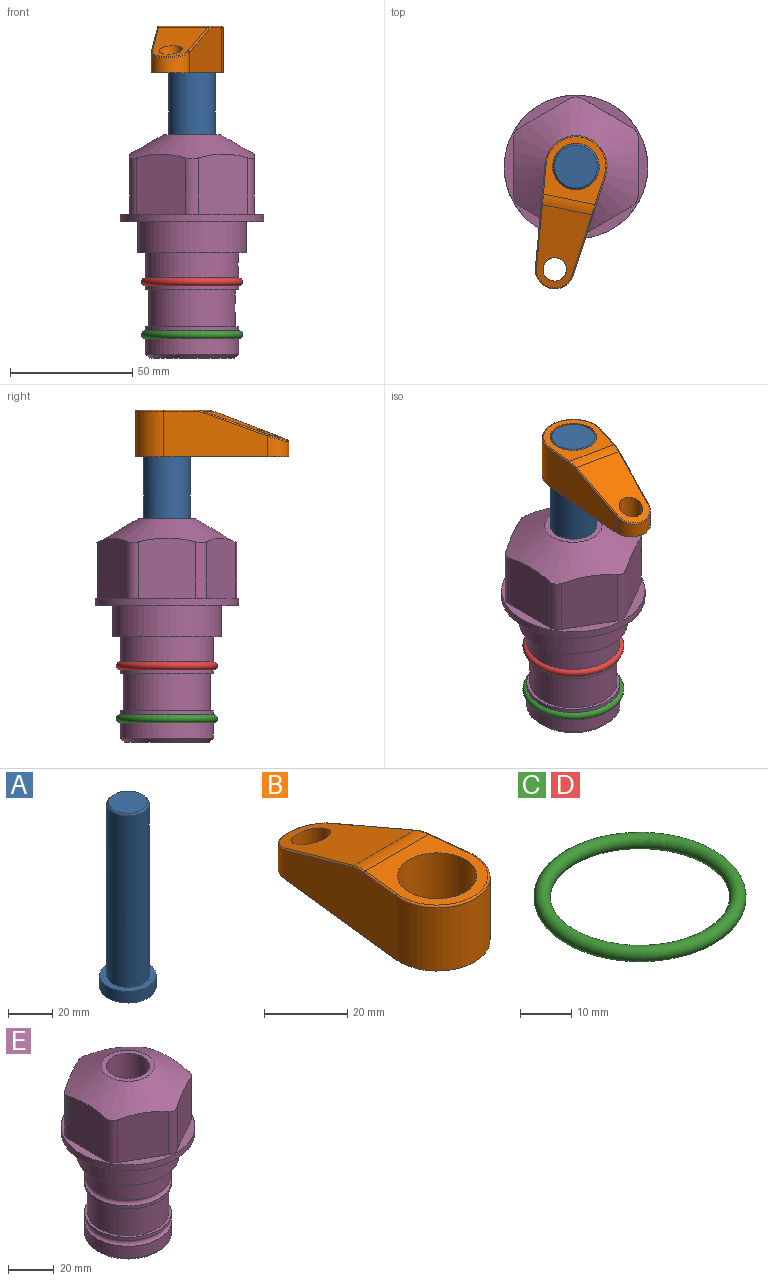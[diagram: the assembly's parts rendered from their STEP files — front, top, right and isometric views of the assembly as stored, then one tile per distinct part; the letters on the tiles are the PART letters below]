
ASSEMBLY  parts=5 mates=3
PART A: 6 faces, bbox 25.4x25.4x101.6 mm
  f0: plane 17.46x17.46mm, normal (0,0,1), area 239.5mm2, adj f5
  f1: plane 25.4x25.4mm, normal (0,0,-1), area 506.7mm2, adj f2
  f2: cylinder r=12.7mm len=25.4mm, axis (0,0,1), area 506.7mm2, adj f1,f3
  f3: plane 25.4x25.4mm, normal (0,0,1), area 221.7mm2, adj f2,f4
  f4: cylinder r=9.53mm len=94.46mm, axis (0,0,1), area 5653mm2, adj f3,f5
  f5: cone r=8.73mm half-angle=45deg, axis (0,0,-1), area 64.4mm2, adj f0,f4
PART B: 44 faces, bbox 27.5x64.5x19.1 mm
  f0: plane 2.3x0.95mm, normal (0,0,-1), area 1mm2, adj f25,f30,f34
  f1: plane 63.5x25.4mm, normal (0,0,-1), area 561.7mm2, adj f2,f3,f4,f5,f6,f7,f19,f20
  f2: cylinder r=12.7mm len=25.4mm, axis (0,0,-1), area 792.2mm2, adj f1,f3,f5,f13
  f3: plane 42.33x18.54mm, normal (0.99,0.11,0), area 647mm2, adj f1,f2,f4,f11,f12,f14
  f4: cylinder r=7.94mm len=15.78mm, axis (0,0,-1), area 158.6mm2, adj f1,f3,f5,f16
  f5: plane 42.33x18.54mm, normal (-0.99,0.11,0), area 647mm2, adj f1,f2,f4,f15,f17,f18
  f6: cylinder r=9.53mm len=19.05mm, axis (0,0,-1), area 1140.1mm2, adj f1,f8
  f7: cylinder r=4.76mm len=10.98mm, axis (0,0,-1), area 276.1mm2, adj f1,f9
  f8: plane 25.83x24.38mm, normal (0,0,1), area 262.2mm2, adj f6,f10,f11,f13,f15
  f9: plane 32.49x20.55mm, normal (0,0.34,0.94), area 489.9mm2, adj f7,f10,f14,f16,f18
  f10: cylinder r=12.7mm len=21.49mm, axis (-1,0,0), area 93.2mm2, adj f8,f9,f12,f17
  f11: cylinder r=0.51mm len=12.34mm, axis (0.11,-0.99,0), area 9.9mm2, adj f3,f8,f12,f13
  f12: bspline ~7.62x1.64mm, area 3.5mm2, adj f3,f10,f11,f14
  f13: torus R=12.19mm, axis (0,0,1), area 33.6mm2, adj f2,f8,f11,f15
  f14: cylinder r=0.51mm len=26.01mm, axis (0.1,-0.93,0.34), area 21.6mm2, adj f3,f9,f12,f16
  f15: cylinder r=0.51mm len=12.34mm, axis (0.11,0.99,0), area 9.9mm2, adj f5,f8,f13,f17
  f16: bspline ~15.78x7.05mm, area 15.7mm2, adj f4,f9,f14,f18
  f17: bspline ~7.62x1.64mm, area 3.5mm2, adj f5,f10,f15,f18
  f18: cylinder r=0.51mm len=26.01mm, axis (0.1,0.93,-0.34), area 21.6mm2, adj f5,f9,f16,f17
  f19: plane 21.6x14.29mm, normal (-0.99,-0.11,0), area 242.6mm2, adj f1,f26,f28,f34,f36,f38
  f20: plane 21.6x14.29mm, normal (0.99,-0.11,0), area 242.6mm2, adj f1,f27,f29,f37,f39,f41
  f21: cylinder r=12.7mm len=14.29mm, axis (0,0,-1), area 173.2mm2, adj f1,f26,f27,f30,f31,f33
  f22: cylinder r=7.94mm len=7.63mm, axis (0,0,-1), area 53.8mm2, adj f1,f28,f29,f42
  f23: plane 2.3x0.95mm, normal (0,0,-1), area 1mm2, adj f25,f33,f37
  f24: plane 17.94x12.32mm, normal (0,-0.34,-0.94), area 191.2mm2, adj f25,f38,f41,f42
  f25: cylinder r=9.53mm len=12.93mm, axis (-1,0,0), area 37.5mm2, adj f0,f23,f24,f31,f36,f39
  f26: cylinder r=1.59mm len=14.29mm, axis (0,0,-1), area 49mm2, adj f1,f19,f21,f32
  f27: cylinder r=1.59mm len=14.29mm, axis (0,0,-1), area 49mm2, adj f1,f20,f21,f35
  f28: cylinder r=1.59mm len=7.28mm, axis (0,0,-1), area 22.1mm2, adj f1,f19,f22,f40
  f29: cylinder r=1.59mm len=7.28mm, axis (0,0,-1), area 22.1mm2, adj f1,f20,f22,f43
  f30: torus R=14.29mm, axis (0,0,1), area 5.8mm2, adj f0,f21,f31,f32
  f31: bspline ~11.06x2.73mm, area 20.8mm2, adj f21,f25,f30,f33
  f32: sphere r=1.59mm, area 5.4mm2, adj f26,f30,f34
  f33: torus R=14.29mm, axis (0,0,1), area 5.8mm2, adj f21,f23,f31,f35
  f34: cylinder r=1.59mm len=1.68mm, axis (-0.11,0.99,0), area 2.4mm2, adj f0,f19,f32,f36
  f35: sphere r=1.59mm, area 5.4mm2, adj f27,f33,f37
  f36: bspline ~5.82x2.33mm, area 7.7mm2, adj f19,f25,f34,f38
  f37: cylinder r=1.59mm len=1.68mm, axis (0.11,0.99,0), area 2.4mm2, adj f20,f23,f35,f39
  f38: cylinder r=1.59mm len=18.33mm, axis (0.1,-0.93,0.34), area 46.7mm2, adj f19,f24,f36,f40
  f39: bspline ~5.82x2.33mm, area 7.7mm2, adj f20,f25,f37,f41
  f40: sphere r=1.59mm, area 3.6mm2, adj f28,f38,f42
  f41: cylinder r=1.59mm len=18.33mm, axis (0.1,0.93,-0.34), area 46.7mm2, adj f20,f24,f39,f43
  f42: bspline ~8.31x1.84mm, area 15.3mm2, adj f22,f24,f40,f43
  f43: sphere r=1.59mm, area 3.6mm2, adj f29,f41,f42
PART C: 1 faces, bbox 44.7x44.7x3.2 mm
  f0: torus R=19.05mm, axis (0,0,1), area 1193.9mm2
PART D: same geometry as C
PART E: 36 faces, bbox 58.7x58.7x91.2 mm
  f0: cylinder r=17.78mm len=35.56mm, axis (0,0,1), area 1670.8mm2, adj f23,f24,f31
  f1: cylinder r=19.05mm len=38.1mm, axis (0,0,1), area 1191.9mm2, adj f26,f27,f30
  f2: plane 58.66x58.66mm, normal (0,0,-1), area 1150.6mm2, adj f3,f28
  f3: cylinder r=29.33mm len=58.66mm, axis (0,0,-1), area 585.1mm2, adj f2,f4
  f4: plane 58.66x58.66mm, normal (0,0,1), area 475.9mm2, adj f3,f5,f6,f7,f8,f9,f10,f11
  f5: plane 24.5x20.32mm, normal (-0.5,0.87,0), area 562.8mm2, adj f4,f15,f16,f17
  f6: plane 24.5x20.32mm, normal (0.5,0.87,0), area 562.8mm2, adj f4,f14,f15,f17
  f7: plane 24.5x23.48mm, normal (1,0,0), area 562.8mm2, adj f4,f13,f14,f17
  f8: plane 24.5x20.32mm, normal (0.5,-0.87,0), area 562.8mm2, adj f4,f12,f13,f17
  f9: plane 24.5x20.32mm, normal (-0.5,-0.87,0), area 562.8mm2, adj f4,f11,f12,f17
  f10: plane 24.5x23.48mm, normal (-1,0,0), area 562.8mm2, adj f4,f11,f16,f17
  f11: cylinder r=5.08mm len=23.01mm, axis (0,0,-1), area 121.2mm2, adj f4,f9,f10,f17
  f12: cylinder r=5.08mm len=23.01mm, axis (0,0,-1), area 121.2mm2, adj f4,f8,f9,f17
  f13: cylinder r=5.08mm len=23.01mm, axis (0,0,-1), area 121.2mm2, adj f4,f7,f8,f17
  f14: cylinder r=5.08mm len=23.01mm, axis (0,0,-1), area 121.2mm2, adj f4,f6,f7,f17
  f15: cylinder r=5.08mm len=23.01mm, axis (0,0,-1), area 121.2mm2, adj f4,f5,f6,f17
  f16: cylinder r=5.08mm len=23.01mm, axis (0,0,-1), area 121.2mm2, adj f4,f5,f10,f17
  f17: cone r=11.73mm half-angle=60deg, axis (0,0,-1), area 2071.8mm2, adj f5,f6,f7,f8,f9,f10,f11,f12
  f18: plane 23.46x23.46mm, normal (0,0,1), area 147.4mm2, adj f17,f35
  f19: plane 34.93x34.93mm, normal (0,0,-1), area 958mm2, adj f29
  f20: cylinder r=19.05mm len=38.1mm, axis (0,0,1), area 760.1mm2, adj f21,f29
  f21: torus R=19.05mm, axis (0,0,1), area 565.3mm2, adj f20,f22
  f22: cylinder r=19.05mm len=38.1mm, axis (0,0,1), area 190mm2, adj f21,f23
  f23: plane 38.1x38.1mm, normal (0,0,1), area 146.9mm2, adj f0,f22
  f24: plane 38.1x38.1mm, normal (0,0,-1), area 146.9mm2, adj f0,f25
  f25: cylinder r=19.05mm len=38.1mm, axis (0,0,1), area 190mm2, adj f24,f26
  f26: torus R=19.05mm, axis (0,0,1), area 565.3mm2, adj f1,f25
  f27: plane 44.45x44.45mm, normal (0,0,-1), area 411.7mm2, adj f1,f28
  f28: cylinder r=22.23mm len=44.45mm, axis (0,0,1), area 1773.5mm2, adj f2,f27
  f29: cone r=19.05mm half-angle=45deg, axis (0,0,1), area 257.5mm2, adj f19,f20
  f30: cylinder r=3.17mm len=6.75mm, axis (-1,0,0), area 128mm2, adj f1,f33
  f31: cylinder r=3.17mm len=6.35mm, axis (-1,0,0), area 102.5mm2, adj f0,f33
  f32: plane 25.4x25.4mm, normal (0,0,1), area 506.7mm2, adj f33
  f33: cylinder r=12.7mm len=66.42mm, axis (0,0,-1), area 5236.2mm2, adj f30,f31,f32,f34
  f34: cone r=9.53mm half-angle=30deg, axis (0,0,-1), area 443.4mm2, adj f33,f35
  f35: cylinder r=9.53mm len=19.05mm, axis (0,0,-1), area 849mm2, adj f18,f34
PLACE A rot(axis=(0,0,-1),101.7deg) t=(0,0,6.38)mm
PLACE B rot(axis=(0,0,1),168.3deg) t=(0,0,60.99)mm
PLACE C t=(0,0,-21.59)mm
PLACE D at identity
PLACE E at identity
MATE fastened C.f0 <-> E.f0  axis (0,0,1) through (0,0,-46.1)mm
MATE cylindrical A.f2 <-> E.f0  axis (0,0,1) through (0,0,32.01)mm
MATE fastened B.f2 <-> A.f2  axis (0,0,1) through (0,0,80.04)mm
